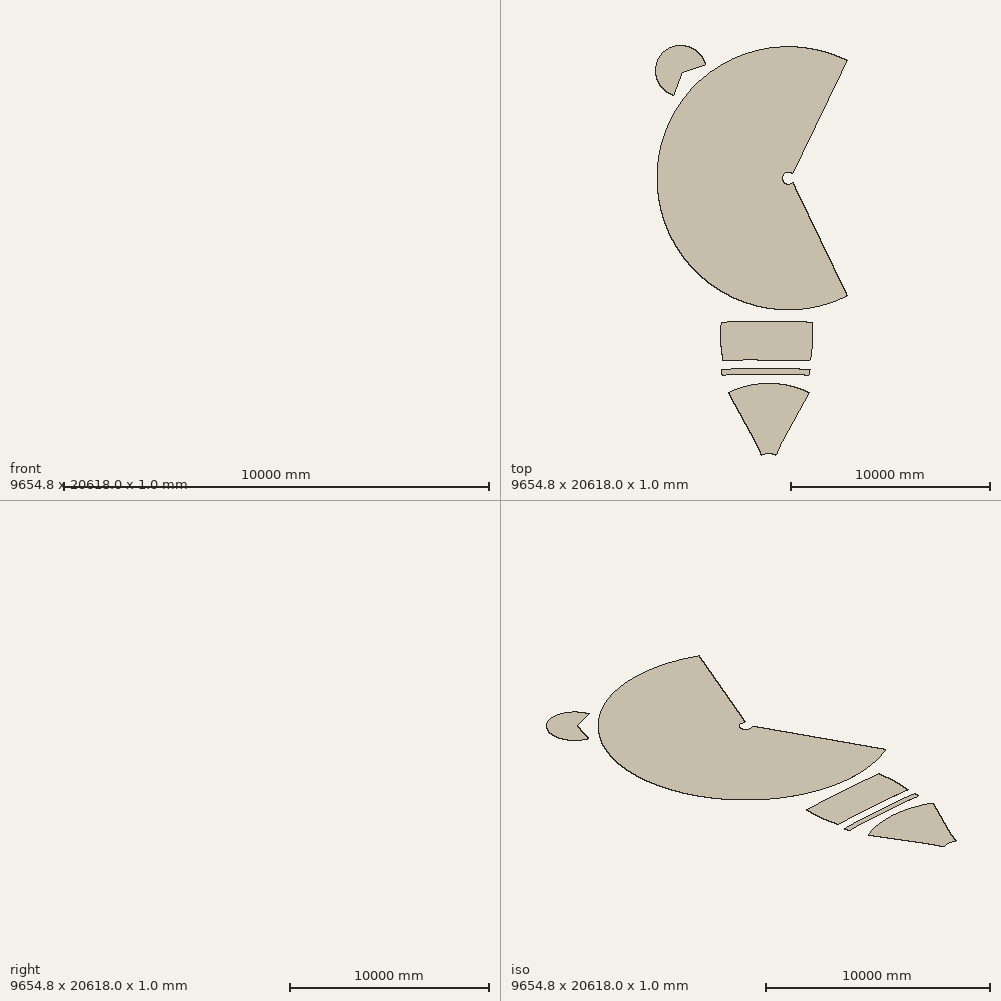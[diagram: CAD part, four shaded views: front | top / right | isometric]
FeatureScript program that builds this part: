
annotation { "Feature Type Name" : "Feature", "Feature Type Description" : "" }
export const myFeature = defineFeature(function(context is Context, id is Id, definition is map)
    precondition{}
    {
        {
            var Q0;
            Q0=qCreatedBy(makeId("Top.planeOp"),FACE);
            var sketch = newSketch(context, id + "F0", { "sketchPlane" : qUnion([Q0])});
            skCircle(sketch, "E0", {"center": v(-2739.04, -542.95) * mm, "radius": 758.26 * mm});
            skCircle(sketch, "E1", {"center": v(-2739.04, -542.95) * mm, "radius": 862.84 * mm});
            skCircle(sketch, "E2", {"center": v(-2739.04, -542.95) * mm, "radius": 425.03 * mm});
            skCircle(sketch, "E3", {"center": v(-2739.04, -542.95) * mm, "radius": 375.03 * mm});
            skCircle(sketch, "E4", {"center": v(-2441.58, -4363.05) * mm, "radius": 425.03 * mm});
            skCircle(sketch, "E5", {"center": v(-2441.58, -5322.2) * mm, "radius": 425.03 * mm});
            skCircle(sketch, "E6", {"center": v(-2591.3, -2491.35) * mm, "radius": 862.84 * mm});
            skCircle(sketch, "E7", {"center": v(-2591.3, -2491.35) * mm, "radius": 758.26 * mm});
            skArc(sketch, "E8", {"start": v(-1201.59, -3471.03) * mm, "mid": v(877.7, -2988.47) * mm, "end": v(2956.98, -3471.03) * mm});
            skLineSegment(sketch, "E9", {"start": v(2956.98, -3471.03) * mm, "end": v(3048.2, -3515.78) * mm});
            skLineSegment(sketch, "E10", {"start": v(3048.2, -3515.78) * mm, "end": v(3002, -3606.28) * mm});
            skLineSegment(sketch, "E11", {"start": v(3002, -3606.28) * mm, "end": v(2531.15, -4495.5) * mm});
            skLineSegment(sketch, "E12", {"start": v(2531.15, -4495.5) * mm, "end": v(1747.82, -5891.78) * mm});
            skLineSegment(sketch, "E13", {"start": v(1747.82, -5891.78) * mm, "end": v(1601.77, -6173.17) * mm});
            skLineSegment(sketch, "E14", {"start": v(1601.77, -6173.17) * mm, "end": v(1533.24, -6315.37) * mm});
            skLineSegment(sketch, "E15", {"start": v(1533.24, -6315.37) * mm, "end": v(1468.57, -6458.87) * mm});
            skLineSegment(sketch, "E16", {"start": v(1468.57, -6458.87) * mm, "end": v(1408.3, -6603.94) * mm});
            skLineSegment(sketch, "E17", {"start": v(1408.3, -6603.94) * mm, "end": v(1352.75, -6750.68) * mm});
            skLineSegment(sketch, "E18", {"start": v(1352.75, -6750.68) * mm, "end": v(1313.39, -6860.16) * mm});
            skLineSegment(sketch, "E19", {"start": v(1313.39, -6860.16) * mm, "end": v(1211.06, -6804.8) * mm});
            skArc(sketch, "E20", {"start": v(1211.06, -6804.8) * mm, "mid": v(877.7, -6720.38) * mm, "end": v(544.33, -6804.8) * mm});
            skLineSegment(sketch, "E21", {"start": v(544.33, -6804.8) * mm, "end": v(442, -6860.16) * mm});
            skLineSegment(sketch, "E22", {"start": v(442, -6860.16) * mm, "end": v(402.64, -6750.68) * mm});
            skLineSegment(sketch, "E23", {"start": v(402.64, -6750.68) * mm, "end": v(347.1, -6603.94) * mm});
            skLineSegment(sketch, "E24", {"start": v(347.1, -6603.94) * mm, "end": v(286.83, -6458.87) * mm});
            skLineSegment(sketch, "E25", {"start": v(286.83, -6458.87) * mm, "end": v(222.15, -6315.37) * mm});
            skLineSegment(sketch, "E26", {"start": v(222.15, -6315.37) * mm, "end": v(153.62, -6173.17) * mm});
            skLineSegment(sketch, "E27", {"start": v(153.62, -6173.17) * mm, "end": v(7.57, -5891.78) * mm});
            skLineSegment(sketch, "E28", {"start": v(7.57, -5891.78) * mm, "end": v(-1080.07, -3929.04) * mm});
            skLineSegment(sketch, "E29", {"start": v(-1080.07, -3929.04) * mm, "end": v(-1246.61, -3606.28) * mm});
            skLineSegment(sketch, "E30", {"start": v(-1246.61, -3606.28) * mm, "end": v(-1292.8, -3515.78) * mm});
            skLineSegment(sketch, "E31", {"start": v(-1292.8, -3515.78) * mm, "end": v(-1201.59, -3471.03) * mm});
            skLineSegment(sketch, "E32", {"start": v(3057.59, -103.9) * mm, "end": v(3081.29, -540.92) * mm});
            skLineSegment(sketch, "E33", {"start": v(3081.29, -540.92) * mm, "end": v(3085.25, -688.56) * mm});
            skLineSegment(sketch, "E34", {"start": v(3085.25, -688.56) * mm, "end": v(3085.2, -836.79) * mm});
            skLineSegment(sketch, "E35", {"start": v(3085.2, -836.79) * mm, "end": v(3080.6, -985.15) * mm});
            skLineSegment(sketch, "E36", {"start": v(3080.6, -985.15) * mm, "end": v(3071.35, -1133.2) * mm});
            skLineSegment(sketch, "E37", {"start": v(3071.35, -1133.2) * mm, "end": v(3057.92, -1280.52) * mm});
            skLineSegment(sketch, "E38", {"start": v(3057.92, -1280.52) * mm, "end": v(3021.78, -1572.28) * mm});
            skLineSegment(sketch, "E39", {"start": v(3021.78, -1572.28) * mm, "end": v(2980.5, -1860.24) * mm});
            skLineSegment(sketch, "E40", {"start": v(2980.5, -1860.24) * mm, "end": v(2967.2, -1953.85) * mm});
            skLineSegment(sketch, "E41", {"start": v(2967.2, -1953.85) * mm, "end": v(2872.99, -1945.8) * mm});
            skLineSegment(sketch, "E42", {"start": v(2872.99, -1945.8) * mm, "end": v(2743.18, -1936.23) * mm});
            skLineSegment(sketch, "E43", {"start": v(2743.18, -1936.23) * mm, "end": v(2612.75, -1929.2) * mm});
            skLineSegment(sketch, "E44", {"start": v(2612.75, -1929.2) * mm, "end": v(2350.26, -1920.48) * mm});
            skLineSegment(sketch, "E45", {"start": v(2350.26, -1920.48) * mm, "end": v(-293.66, -1912.57) * mm});
            skLineSegment(sketch, "E46", {"start": v(-293.66, -1912.57) * mm, "end": v(-821.6, -1920.48) * mm});
            skLineSegment(sketch, "E47", {"start": v(-821.6, -1920.48) * mm, "end": v(-1084.1, -1929.2) * mm});
            skLineSegment(sketch, "E48", {"start": v(-1084.1, -1929.2) * mm, "end": v(-1214.51, -1936.23) * mm});
            skLineSegment(sketch, "E49", {"start": v(-1214.51, -1936.23) * mm, "end": v(-1344.33, -1945.8) * mm});
            skLineSegment(sketch, "E50", {"start": v(-1344.33, -1945.8) * mm, "end": v(-1438.54, -1953.85) * mm});
            skLineSegment(sketch, "E51", {"start": v(-1438.54, -1953.85) * mm, "end": v(-1451.84, -1860.24) * mm});
            skLineSegment(sketch, "E52", {"start": v(-1451.84, -1860.24) * mm, "end": v(-1493.12, -1572.28) * mm});
            skLineSegment(sketch, "E53", {"start": v(-1493.12, -1572.28) * mm, "end": v(-1529.26, -1280.52) * mm});
            skLineSegment(sketch, "E54", {"start": v(-1529.26, -1280.52) * mm, "end": v(-1542.69, -1133.2) * mm});
            skLineSegment(sketch, "E55", {"start": v(-1542.69, -1133.2) * mm, "end": v(-1551.94, -985.15) * mm});
            skLineSegment(sketch, "E56", {"start": v(-1551.94, -985.15) * mm, "end": v(-1556.53, -836.79) * mm});
            skLineSegment(sketch, "E57", {"start": v(-1556.53, -836.79) * mm, "end": v(-1556.6, -688.56) * mm});
            skLineSegment(sketch, "E58", {"start": v(-1556.6, -688.56) * mm, "end": v(-1552.62, -540.92) * mm});
            skLineSegment(sketch, "E59", {"start": v(-1552.62, -540.92) * mm, "end": v(-1528.92, -103.9) * mm});
            skLineSegment(sketch, "E60", {"start": v(-1528.92, -103.9) * mm, "end": v(-1523.66, -10.18) * mm});
            skLineSegment(sketch, "E61", {"start": v(-1523.66, -10.18) * mm, "end": v(-1429.8, -9.5) * mm});
            skLineSegment(sketch, "E62", {"start": v(-1429.8, -9.5) * mm, "end": v(256.6, 40.27) * mm});
            skLineSegment(sketch, "E63", {"start": v(256.6, 40.27) * mm, "end": v(1272.07, 40.27) * mm});
            skLineSegment(sketch, "E64", {"start": v(1272.07, 40.27) * mm, "end": v(2958.46, -9.5) * mm});
            skLineSegment(sketch, "E65", {"start": v(2958.46, -9.5) * mm, "end": v(3052.32, -10.18) * mm});
            skLineSegment(sketch, "E66", {"start": v(3052.32, -10.18) * mm, "end": v(3057.59, -103.9) * mm});
            skLineSegment(sketch, "E67", {"start": v(2808.33, -2683.67) * mm, "end": v(2718.14, -2672.93) * mm});
            skLineSegment(sketch, "E68", {"start": v(2718.14, -2672.93) * mm, "end": v(2632.86, -2664.54) * mm});
            skLineSegment(sketch, "E69", {"start": v(2632.86, -2664.54) * mm, "end": v(2461.42, -2652.15) * mm});
            skLineSegment(sketch, "E70", {"start": v(2461.42, -2652.15) * mm, "end": v(2288.95, -2644.68) * mm});
            skLineSegment(sketch, "E71", {"start": v(2288.95, -2644.68) * mm, "end": v(2115.63, -2640.98) * mm});
            skLineSegment(sketch, "E72", {"start": v(2115.63, -2640.98) * mm, "end": v(-684.56, -2640.98) * mm});
            skLineSegment(sketch, "E73", {"start": v(-684.56, -2640.98) * mm, "end": v(-857.88, -2644.68) * mm});
            skLineSegment(sketch, "E74", {"start": v(-857.88, -2644.68) * mm, "end": v(-1030.34, -2652.15) * mm});
            skLineSegment(sketch, "E75", {"start": v(-1030.34, -2652.15) * mm, "end": v(-1201.79, -2664.54) * mm});
            skLineSegment(sketch, "E76", {"start": v(-1201.79, -2664.54) * mm, "end": v(-1287.07, -2672.93) * mm});
            skLineSegment(sketch, "E77", {"start": v(-1287.07, -2672.93) * mm, "end": v(-1377.26, -2683.67) * mm});
            skLineSegment(sketch, "E78", {"start": v(-1377.26, -2683.67) * mm, "end": v(-1476.68, -2696.65) * mm});
            skLineSegment(sketch, "E79", {"start": v(-1476.68, -2696.65) * mm, "end": v(-1489.4, -2597.2) * mm});
            skLineSegment(sketch, "E80", {"start": v(-1489.4, -2597.2) * mm, "end": v(-1500.02, -2514.21) * mm});
            skLineSegment(sketch, "E81", {"start": v(-1500.02, -2514.21) * mm, "end": v(-1512.7, -2415.13) * mm});
            skLineSegment(sketch, "E82", {"start": v(-1512.7, -2415.13) * mm, "end": v(-1413.63, -2402.34) * mm});
            skLineSegment(sketch, "E83", {"start": v(-1413.63, -2402.34) * mm, "end": v(-1323.96, -2391.7) * mm});
            skLineSegment(sketch, "E84", {"start": v(-1323.96, -2391.7) * mm, "end": v(-1234.3, -2382.81) * mm});
            skLineSegment(sketch, "E85", {"start": v(-1234.3, -2382.81) * mm, "end": v(-1055.12, -2369.7) * mm});
            skLineSegment(sketch, "E86", {"start": v(-1055.12, -2369.7) * mm, "end": v(-876.26, -2361.74) * mm});
            skLineSegment(sketch, "E87", {"start": v(-876.26, -2361.74) * mm, "end": v(-697.9, -2357.76) * mm});
            skLineSegment(sketch, "E88", {"start": v(-697.9, -2357.76) * mm, "end": v(2128.97, -2357.76) * mm});
            skLineSegment(sketch, "E89", {"start": v(2128.97, -2357.76) * mm, "end": v(2307.33, -2361.74) * mm});
            skLineSegment(sketch, "E90", {"start": v(2307.33, -2361.74) * mm, "end": v(2486.2, -2369.7) * mm});
            skLineSegment(sketch, "E91", {"start": v(2486.2, -2369.7) * mm, "end": v(2665.38, -2382.81) * mm});
            skLineSegment(sketch, "E92", {"start": v(2665.38, -2382.81) * mm, "end": v(2755.04, -2391.7) * mm});
            skLineSegment(sketch, "E93", {"start": v(2755.04, -2391.7) * mm, "end": v(2844.7, -2402.34) * mm});
            skLineSegment(sketch, "E94", {"start": v(2844.7, -2402.34) * mm, "end": v(2943.78, -2415.13) * mm});
            skLineSegment(sketch, "E95", {"start": v(2943.78, -2415.13) * mm, "end": v(2931.1, -2514.21) * mm});
            skLineSegment(sketch, "E96", {"start": v(2931.1, -2514.21) * mm, "end": v(2920.47, -2597.2) * mm});
            skLineSegment(sketch, "E97", {"start": v(2920.47, -2597.2) * mm, "end": v(2907.75, -2696.65) * mm});
            skLineSegment(sketch, "E98", {"start": v(2907.75, -2696.65) * mm, "end": v(2808.33, -2683.67) * mm});
            skLineSegment(sketch, "E99", {"start": v(2881.5, -1846.17) * mm, "end": v(2749.47, -1836.42) * mm});
            skLineSegment(sketch, "E100", {"start": v(2749.47, -1836.42) * mm, "end": v(2617.3, -1829.3) * mm});
            skLineSegment(sketch, "E101", {"start": v(2617.3, -1829.3) * mm, "end": v(2352.67, -1820.5) * mm});
            skLineSegment(sketch, "E102", {"start": v(2352.67, -1820.5) * mm, "end": v(764.33, -1808.9) * mm});
            skLineSegment(sketch, "E103", {"start": v(764.33, -1808.9) * mm, "end": v(-824, -1820.5) * mm});
            skLineSegment(sketch, "E104", {"start": v(-824, -1820.5) * mm, "end": v(-1088.63, -1829.3) * mm});
            skLineSegment(sketch, "E105", {"start": v(-1088.63, -1829.3) * mm, "end": v(-1220.81, -1836.42) * mm});
            skLineSegment(sketch, "E106", {"start": v(-1220.81, -1836.42) * mm, "end": v(-1352.84, -1846.17) * mm});
            skLineSegment(sketch, "E107", {"start": v(-1429.08, -109.5) * mm, "end": v(257.99, -59.72) * mm});
            skLineSegment(sketch, "E108", {"start": v(257.99, -59.72) * mm, "end": v(764.33, -56.16) * mm});
            skLineSegment(sketch, "E109", {"start": v(764.33, -56.16) * mm, "end": v(1945.64, -75.2) * mm});
            skLineSegment(sketch, "E110", {"start": v(1945.64, -75.2) * mm, "end": v(2957.74, -109.5) * mm});
            skLineSegment(sketch, "E111", {"start": v(-1352.84, -1846.17) * mm, "end": v(-1394.07, -1558.53) * mm});
            skLineSegment(sketch, "E112", {"start": v(-1394.07, -1558.53) * mm, "end": v(-1429.8, -1270.16) * mm});
            skLineSegment(sketch, "E113", {"start": v(-1429.8, -1270.16) * mm, "end": v(-1442.99, -1125.47) * mm});
            skLineSegment(sketch, "E114", {"start": v(-1442.99, -1125.47) * mm, "end": v(-1452.05, -980.47) * mm});
            skLineSegment(sketch, "E115", {"start": v(-1452.05, -980.47) * mm, "end": v(-1456.54, -835.26) * mm});
            skLineSegment(sketch, "E116", {"start": v(-1456.54, -835.26) * mm, "end": v(-1456.6, -689.97) * mm});
            skLineSegment(sketch, "E117", {"start": v(-1456.6, -689.97) * mm, "end": v(-1452.7, -544.74) * mm});
            skLineSegment(sketch, "E118", {"start": v(-1452.7, -544.74) * mm, "end": v(-1429.08, -109.5) * mm});
            skLineSegment(sketch, "E119", {"start": v(2881.5, -1846.17) * mm, "end": v(2922.73, -1558.53) * mm});
            skLineSegment(sketch, "E120", {"start": v(2922.73, -1558.53) * mm, "end": v(2958.46, -1270.16) * mm});
            skLineSegment(sketch, "E121", {"start": v(2958.46, -1270.16) * mm, "end": v(2971.65, -1125.47) * mm});
            skLineSegment(sketch, "E122", {"start": v(2971.65, -1125.47) * mm, "end": v(2980.72, -980.47) * mm});
            skLineSegment(sketch, "E123", {"start": v(2980.72, -980.47) * mm, "end": v(2985.2, -835.26) * mm});
            skLineSegment(sketch, "E124", {"start": v(2985.2, -835.26) * mm, "end": v(2985.26, -689.97) * mm});
            skLineSegment(sketch, "E125", {"start": v(2985.26, -689.97) * mm, "end": v(2981.36, -544.74) * mm});
            skLineSegment(sketch, "E126", {"start": v(2981.36, -544.74) * mm, "end": v(2957.74, -109.5) * mm});
            skLineSegment(sketch, "E127", {"start": v(2821.28, -2584.5) * mm, "end": v(2728.9, -2573.51) * mm});
            skLineSegment(sketch, "E128", {"start": v(2728.9, -2573.51) * mm, "end": v(2641.74, -2564.93) * mm});
            skLineSegment(sketch, "E129", {"start": v(2641.74, -2564.93) * mm, "end": v(2467.07, -2552.3) * mm});
            skLineSegment(sketch, "E130", {"start": v(2467.07, -2552.3) * mm, "end": v(2292.07, -2544.73) * mm});
            skLineSegment(sketch, "E131", {"start": v(2292.07, -2544.73) * mm, "end": v(2116.9, -2540.99) * mm});
            skLineSegment(sketch, "E132", {"start": v(2116.9, -2540.99) * mm, "end": v(715.54, -2549.02) * mm});
            skLineSegment(sketch, "E133", {"start": v(715.54, -2549.02) * mm, "end": v(-685.83, -2540.99) * mm});
            skLineSegment(sketch, "E134", {"start": v(-685.83, -2540.99) * mm, "end": v(-861, -2544.73) * mm});
            skLineSegment(sketch, "E135", {"start": v(-861, -2544.73) * mm, "end": v(-1036, -2552.3) * mm});
            skLineSegment(sketch, "E136", {"start": v(-1036, -2552.3) * mm, "end": v(-1210.67, -2564.93) * mm});
            skLineSegment(sketch, "E137", {"start": v(-1210.67, -2564.93) * mm, "end": v(-1297.82, -2573.51) * mm});
            skLineSegment(sketch, "E138", {"start": v(-1297.82, -2573.51) * mm, "end": v(-1390.21, -2584.5) * mm});
            skLineSegment(sketch, "E139", {"start": v(-1400.83, -2501.52) * mm, "end": v(-1313.17, -2491.12) * mm});
            skLineSegment(sketch, "E140", {"start": v(-1313.17, -2491.12) * mm, "end": v(-1225.35, -2482.41) * mm});
            skLineSegment(sketch, "E141", {"start": v(-1225.35, -2482.41) * mm, "end": v(-1049.36, -2469.53) * mm});
            skLineSegment(sketch, "E142", {"start": v(-1049.36, -2469.53) * mm, "end": v(-873.04, -2461.7) * mm});
            skLineSegment(sketch, "E143", {"start": v(-873.04, -2461.7) * mm, "end": v(-696.55, -2457.75) * mm});
            skLineSegment(sketch, "E144", {"start": v(-696.55, -2457.75) * mm, "end": v(715.54, -2465.6) * mm});
            skLineSegment(sketch, "E145", {"start": v(715.54, -2465.6) * mm, "end": v(2127.62, -2457.75) * mm});
            skLineSegment(sketch, "E146", {"start": v(2127.62, -2457.75) * mm, "end": v(2304.1, -2461.7) * mm});
            skLineSegment(sketch, "E147", {"start": v(2304.1, -2461.7) * mm, "end": v(2480.43, -2469.53) * mm});
            skLineSegment(sketch, "E148", {"start": v(2480.43, -2469.53) * mm, "end": v(2656.42, -2482.41) * mm});
            skLineSegment(sketch, "E149", {"start": v(2656.42, -2482.41) * mm, "end": v(2744.24, -2491.12) * mm});
            skLineSegment(sketch, "E150", {"start": v(2744.24, -2491.12) * mm, "end": v(2831.9, -2501.52) * mm});
            skLineSegment(sketch, "E151", {"start": v(-1390.21, -2584.5) * mm, "end": v(-1400.83, -2501.52) * mm});
            skArc(sketch, "E152", {"start": v(2912.94, -3560.81) * mm, "mid": v(877.7, -3088.47) * mm, "end": v(-1157.55, -3560.81) * mm});
            skLineSegment(sketch, "E153", {"start": v(1258.65, -6716.85) * mm, "end": v(1315.36, -6567.02) * mm});
            skLineSegment(sketch, "E154", {"start": v(1315.36, -6567.02) * mm, "end": v(1376.82, -6419.09) * mm});
            skLineSegment(sketch, "E155", {"start": v(1376.82, -6419.09) * mm, "end": v(1442.64, -6273.05) * mm});
            skLineSegment(sketch, "E156", {"start": v(1442.64, -6273.05) * mm, "end": v(1512.19, -6128.74) * mm});
            skLineSegment(sketch, "E157", {"start": v(1512.19, -6128.74) * mm, "end": v(1659.78, -5844.37) * mm});
            skLineSegment(sketch, "E158", {"start": v(1659.78, -5844.37) * mm, "end": v(2746.84, -3882.72) * mm});
            skLineSegment(sketch, "E159", {"start": v(2746.84, -3882.72) * mm, "end": v(2912.94, -3560.81) * mm});
            skLineSegment(sketch, "E160", {"start": v(496.74, -6716.85) * mm, "end": v(440.04, -6567.02) * mm});
            skLineSegment(sketch, "E161", {"start": v(440.04, -6567.02) * mm, "end": v(378.57, -6419.09) * mm});
            skLineSegment(sketch, "E162", {"start": v(378.57, -6419.09) * mm, "end": v(312.76, -6273.05) * mm});
            skLineSegment(sketch, "E163", {"start": v(312.76, -6273.05) * mm, "end": v(243.2, -6128.74) * mm});
            skLineSegment(sketch, "E164", {"start": v(243.2, -6128.74) * mm, "end": v(95.62, -5844.37) * mm});
            skLineSegment(sketch, "E165", {"start": v(95.62, -5844.37) * mm, "end": v(-991.44, -3882.72) * mm});
            skLineSegment(sketch, "E166", {"start": v(-991.44, -3882.72) * mm, "end": v(-1157.55, -3560.81) * mm});
            skArc(sketch, "E167", {"start": v(1258.65, -6716.85) * mm, "mid": v(877.7, -6620.38) * mm, "end": v(496.74, -6716.85) * mm});
            skLineSegment(sketch, "E168", {"start": v(2821.28, -2584.5) * mm, "end": v(2831.9, -2501.52) * mm});
            skArc(sketch, "E169", {"start": v(4693.92, 13096.97) * mm, "mid": v(-4653.05, 7222.46) * mm, "end": v(4693.92, 1347.95) * mm});
            skArc(sketch, "E170", {"start": v(2039.96, 7582.88) * mm, "mid": v(1466.49, 7222.46) * mm, "end": v(2039.96, 6862.03) * mm});
            skLineSegment(sketch, "E171", {"start": v(4693.92, 1347.95) * mm, "end": v(2039.96, 6862.03) * mm});
            skLineSegment(sketch, "E172", {"start": v(2039.96, 7582.88) * mm, "end": v(4693.92, 13096.97) * mm});
            skLineSegment(sketch, "E173", {"start": v(2130.07, 7539.52) * mm, "end": v(4784.03, 13053.6) * mm});
            skLineSegment(sketch, "E174", {"start": v(4784.03, 13053.6) * mm, "end": v(4827.4, 13143.71) * mm});
            skLineSegment(sketch, "E175", {"start": v(4827.4, 13143.71) * mm, "end": v(4737.3, 13187.08) * mm});
            skArc(sketch, "E176", {"start": v(4737.3, 13187.08) * mm, "mid": v(-4753.05, 7222.46) * mm, "end": v(4737.3, 1257.84) * mm});
            skLineSegment(sketch, "E177", {"start": v(4737.3, 1257.84) * mm, "end": v(4827.4, 1301.2) * mm});
            skLineSegment(sketch, "E178", {"start": v(4827.4, 1301.2) * mm, "end": v(4784.03, 1391.31) * mm});
            skLineSegment(sketch, "E179", {"start": v(4784.03, 1391.31) * mm, "end": v(2130.07, 6905.4) * mm});
            skLineSegment(sketch, "E180", {"start": v(2130.07, 6905.4) * mm, "end": v(2086.7, 6995.5) * mm});
            skLineSegment(sketch, "E181", {"start": v(2086.7, 6995.5) * mm, "end": v(1996.6, 6952.14) * mm});
            skArc(sketch, "E182", {"start": v(1996.6, 6952.14) * mm, "mid": v(1566.49, 7222.46) * mm, "end": v(1996.6, 7492.78) * mm});
            skLineSegment(sketch, "E183", {"start": v(1996.6, 7492.78) * mm, "end": v(2086.7, 7449.4) * mm});
            skLineSegment(sketch, "E184", {"start": v(2086.7, 7449.4) * mm, "end": v(2130.07, 7539.52) * mm});
            skLineSegment(sketch, "E185", {"start": v(-3470.7, 12541.62) * mm, "end": v(-2396.2, 12896.22) * mm});
            skLineSegment(sketch, "E186", {"start": v(-2396.2, 12896.22) * mm, "end": v(-2301.23, 12927.56) * mm});
            skLineSegment(sketch, "E187", {"start": v(-2301.23, 12927.56) * mm, "end": v(-2332.57, 13022.52) * mm});
            skArc(sketch, "E188", {"start": v(-2332.57, 13022.52) * mm, "mid": v(-4436.1, 13542.54) * mm, "end": v(-3992.4, 11421.6) * mm});
            skLineSegment(sketch, "E189", {"start": v(-3992.4, 11421.6) * mm, "end": v(-3898.63, 11386.84) * mm});
            skLineSegment(sketch, "E190", {"start": v(-3898.63, 11386.84) * mm, "end": v(-3863.88, 11480.61) * mm});
            skLineSegment(sketch, "E191", {"start": v(-3863.88, 11480.61) * mm, "end": v(-3470.7, 12541.62) * mm});
            skLineSegment(sketch, "E192", {"start": v(-3547.75, 12621.5) * mm, "end": v(-2427.53, 12991.18) * mm});
            skArc(sketch, "E193", {"start": v(-2427.53, 12991.18) * mm, "mid": v(-4366.69, 13470.56) * mm, "end": v(-3957.65, 11515.36) * mm});
            skLineSegment(sketch, "E194", {"start": v(-3957.65, 11515.36) * mm, "end": v(-3547.75, 12621.5) * mm});
            skSolve(sketch);
        }
        {
            var Q0;
            Q0=makeQuery(id+"F0.imprint","IMPRINT",FACE,{"disambiguationData":[TD([[makeQuery(id+"F0.imprint","IMPRINT",EDGE,{"derivedFrom":sQuery(id+"F0.wireOp",EDGE,"E32")}),-1.0]])]});
            var Q1;
            Q1=makeQuery(id+"F0.imprint","IMPRINT",FACE,{"disambiguationData":[TD([[makeQuery(id+"F0.imprint","IMPRINT",EDGE,{"derivedFrom":sQuery(id+"F0.wireOp",EDGE,"E99")}),-1.0]])]});
            extrude(context, id + "F1", {"entities" : qUnion([Q0, Q1]), "depth" : 1 * mm, "offsetDistance" : 25 * mm});
        }
        {
            var Q0;
            Q0=makeQuery(id+"F0.imprint","IMPRINT",FACE,{"disambiguationData":[TD([[makeQuery(id+"F0.imprint","IMPRINT",EDGE,{"derivedFrom":sQuery(id+"F0.wireOp",EDGE,"E8")}),-1.0]])]});
            var Q1;
            Q1=makeQuery(id+"F0.imprint","IMPRINT",FACE,{"disambiguationData":[TD([[makeQuery(id+"F0.imprint","IMPRINT",EDGE,{"derivedFrom":sQuery(id+"F0.wireOp",EDGE,"E152")}),1.0]])]});
            extrude(context, id + "F2", {"entities" : qUnion([Q0, Q1]), "depth" : 1 * mm, "offsetDistance" : 25 * mm});
        }
        {
            var Q0;
            Q0=makeQuery(id+"F0.imprint","IMPRINT",FACE,{"disambiguationData":[TD([[makeQuery(id+"F0.imprint","IMPRINT",EDGE,{"derivedFrom":sQuery(id+"F0.wireOp",EDGE,"E169")}),1.0]])]});
            var Q1;
            Q1=makeQuery(id+"F0.imprint","IMPRINT",FACE,{"disambiguationData":[TD([[makeQuery(id+"F0.imprint","IMPRINT",EDGE,{"derivedFrom":sQuery(id+"F0.wireOp",EDGE,"E169")}),-1.0]])]});
            extrude(context, id + "F3", {"entities" : qUnion([Q0, Q1]), "depth" : 1 * mm, "offsetDistance" : 25 * mm});
        }
        {
            var Q0;
            Q0=makeQuery(id+"F0.imprint","IMPRINT",FACE,{"disambiguationData":[TD([[makeQuery(id+"F0.imprint","IMPRINT",EDGE,{"derivedFrom":sQuery(id+"F0.wireOp",EDGE,"E192")}),1.0]])]});
            var Q1;
            Q1=makeQuery(id+"F0.imprint","IMPRINT",FACE,{"disambiguationData":[TD([[makeQuery(id+"F0.imprint","IMPRINT",EDGE,{"derivedFrom":sQuery(id+"F0.wireOp",EDGE,"E185")}),1.0]])]});
            extrude(context, id + "F4", {"entities" : qUnion([Q0, Q1]), "depth" : 1 * mm, "offsetDistance" : 25 * mm});
        }
        {
            var Q0;
            Q0=makeQuery(id+"F0.imprint","IMPRINT",FACE,{"disambiguationData":[TD([[makeQuery(id+"F0.imprint","IMPRINT",EDGE,{"derivedFrom":sQuery(id+"F0.wireOp",EDGE,"E127")}),-1.0]])]});
            var Q1;
            Q1=makeQuery(id+"F0.imprint","IMPRINT",FACE,{"disambiguationData":[TD([[makeQuery(id+"F0.imprint","IMPRINT",EDGE,{"derivedFrom":sQuery(id+"F0.wireOp",EDGE,"E67")}),-1.0]])]});
            extrude(context, id + "F5", {"entities" : qUnion([Q0, Q1]), "depth" : 1 * mm, "offsetDistance" : 25 * mm});
        }
    });
